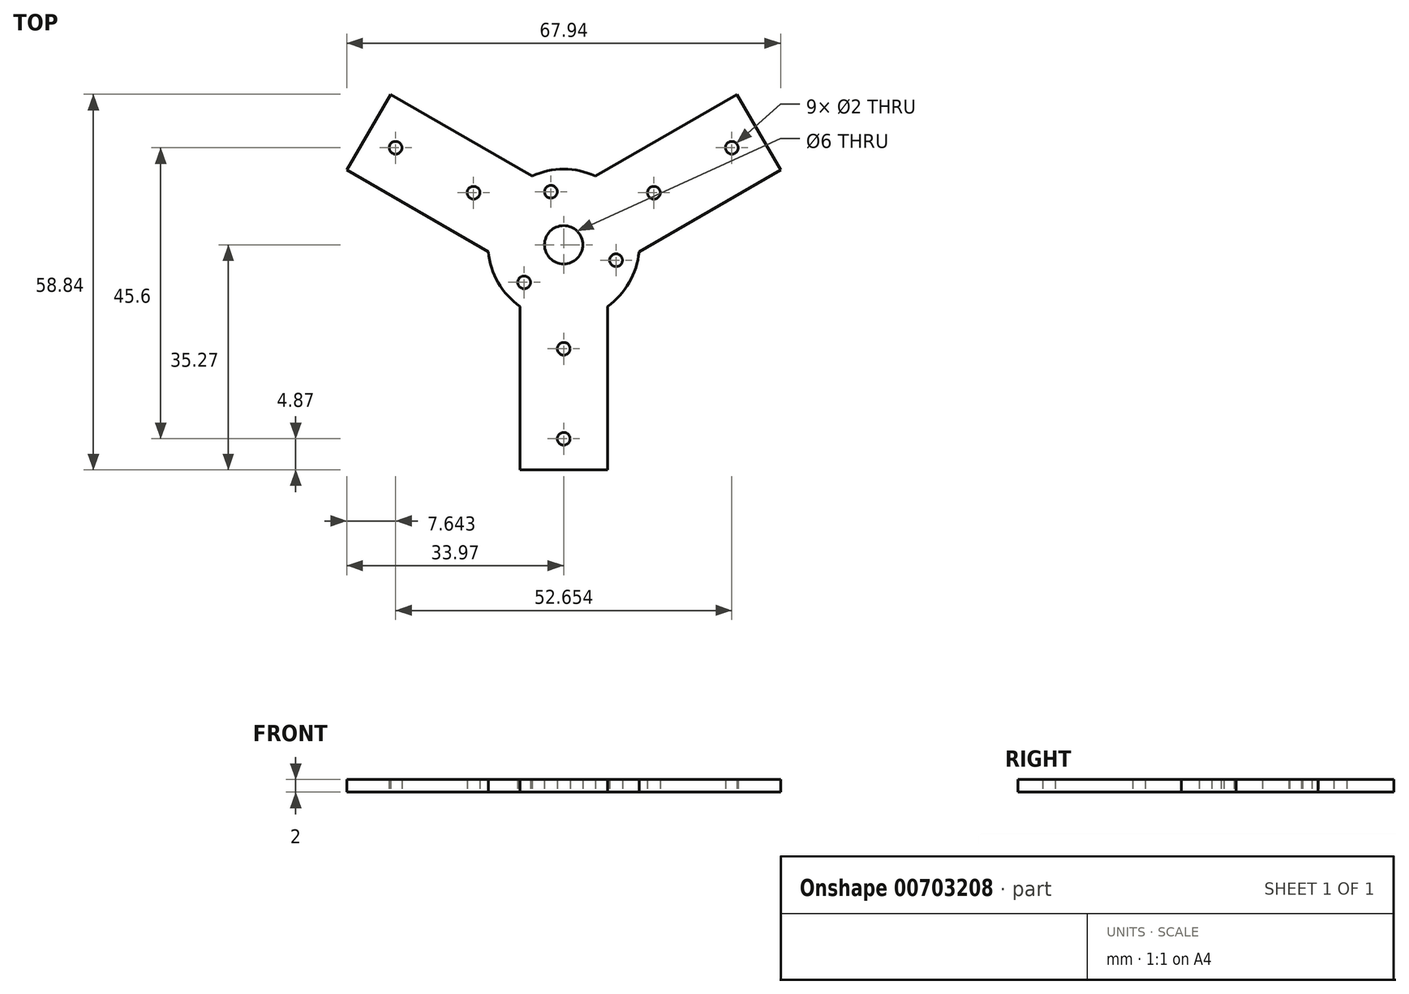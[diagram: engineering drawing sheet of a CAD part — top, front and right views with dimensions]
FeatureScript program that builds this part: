
annotation { "Feature Type Name" : "Feature", "Feature Type Description" : "" }
export const myFeature = defineFeature(function(context is Context, id is Id, definition is map)
    precondition{}
    {
        {
            var Q0;
            Q0=qCreatedBy(makeId("Top.planeOp"),FACE);
            var sketch = newSketch(context, id + "F0", { "sketchPlane" : qUnion([Q0])});
            skArc(sketch, "E0", {"start": v(6.85, -9.67) * mm, "mid": v(10.26, -5.92) * mm, "end": v(11.8, -1.1) * mm});
            skLineSegment(sketch, "E1.top", {"start": v(-6.85, -35.27) * mm, "end": v(6.85, -35.27) * mm});
            skLineSegment(sketch, "E1.left", {"start": v(-6.85, -9.67) * mm, "end": v(-6.85, -35.27) * mm});
            skLineSegment(sketch, "E1.right", {"start": v(6.85, -9.67) * mm, "end": v(6.85, -35.27) * mm});
            skPoint(sketch, "E2.orphan", {"position": v(-6.85, 0) * mm});
            skCircle(sketch, "E3", {"center": v(0, 0) * mm, "radius": 8.55 * mm, "construction": true});
            skCircle(sketch, "E4", {"center": v(-2, 8.31) * mm, "radius": 1 * mm});
            skCircle(sketch, "E5.1.0", {"center": v(-6.2, -5.89) * mm, "radius": 1 * mm});
            skCircle(sketch, "E5.2.0", {"center": v(8.2, -2.42) * mm, "radius": 1 * mm});
            skCircle(sketch, "E6", {"center": v(0, -30.4) * mm, "radius": 1 * mm});
            skCircle(sketch, "E7", {"center": v(0, -16.3) * mm, "radius": 1 * mm});
            skLineSegment(sketch, "E8.1.0", {"start": v(11.8, -1.1) * mm, "end": v(33.97, 11.7) * mm});
            skLineSegment(sketch, "E8.1.1", {"start": v(33.97, 11.7) * mm, "end": v(27.12, 23.57) * mm});
            skCircle(sketch, "E8.1.2", {"center": v(26.33, 15.2) * mm, "radius": 1 * mm});
            skCircle(sketch, "E8.1.3", {"center": v(14.12, 8.15) * mm, "radius": 1 * mm});
            skLineSegment(sketch, "E8.1.4", {"start": v(4.95, 10.77) * mm, "end": v(27.12, 23.57) * mm});
            skLineSegment(sketch, "E8.2.0", {"start": v(-4.95, 10.77) * mm, "end": v(-27.12, 23.57) * mm});
            skLineSegment(sketch, "E8.2.1", {"start": v(-27.12, 23.57) * mm, "end": v(-33.97, 11.7) * mm});
            skCircle(sketch, "E8.2.2", {"center": v(-26.33, 15.2) * mm, "radius": 1 * mm});
            skCircle(sketch, "E8.2.3", {"center": v(-14.12, 8.15) * mm, "radius": 1 * mm});
            skLineSegment(sketch, "E8.2.4", {"start": v(-11.8, -1.1) * mm, "end": v(-33.97, 11.7) * mm});
            skArc(sketch, "E9.trimOffspring", {"start": v(-11.8, -1.1) * mm, "mid": v(-10.26, -5.92) * mm, "end": v(-6.85, -9.67) * mm});
            skArc(sketch, "E10.trimOffspring", {"start": v(4.95, 10.77) * mm, "mid": v(0, 11.85) * mm, "end": v(-4.95, 10.77) * mm});
            skCircle(sketch, "E11", {"center": v(0, 0) * mm, "radius": 3 * mm});
            skSolve(sketch);
        }
        {
            var Q0;
            Q0=makeQuery(id+"F0.imprint","IMPRINT",FACE,{"disambiguationData":[TD([[makeQuery(id+"F0.imprint","IMPRINT",EDGE,{"derivedFrom":sQuery(id+"F0.wireOp",EDGE,"E0")}),1.0]])]});
            extrude(context, id + "F1", {"entities" : qUnion([Q0]), "depth" : 2 * mm, "offsetDistance" : 25 * mm});
        }
    });
